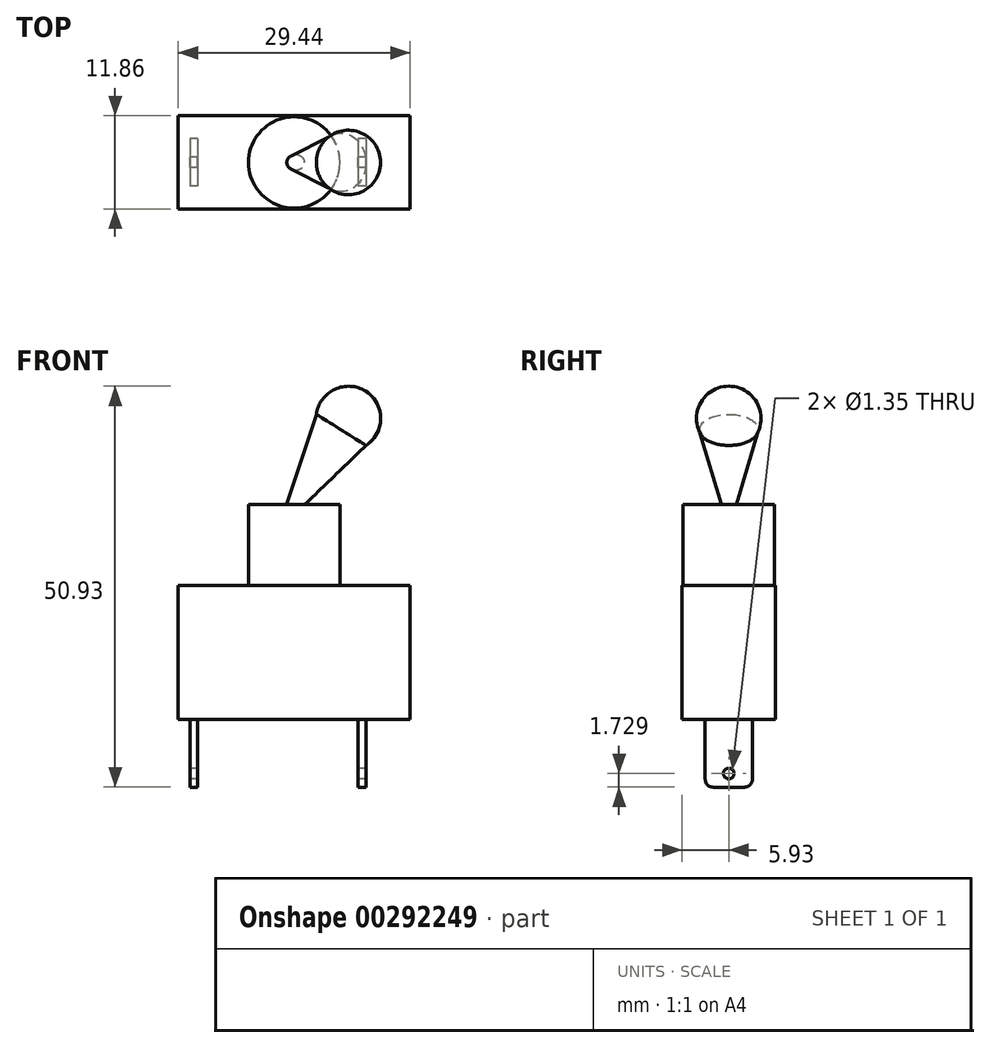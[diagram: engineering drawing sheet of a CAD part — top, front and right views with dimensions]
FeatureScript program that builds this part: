
annotation { "Feature Type Name" : "Feature", "Feature Type Description" : "" }
export const myFeature = defineFeature(function(context is Context, id is Id, definition is map)
    precondition{}
    {
        {
            var Q0;
            Q0=qCreatedBy(makeId("Front.planeOp"),FACE);
            var sketch = newSketch(context, id + "F0", { "sketchPlane" : qUnion([Q0])});
            skLineSegment(sketch, "E0.bottom", {"start": v(14.72, -8.52) * mm, "end": v(-14.72, -8.52) * mm});
            skLineSegment(sketch, "E0.top", {"start": v(14.72, 8.52) * mm, "end": v(-14.72, 8.52) * mm});
            skLineSegment(sketch, "E0.left", {"start": v(14.72, -8.52) * mm, "end": v(14.72, 8.52) * mm});
            skLineSegment(sketch, "E0.right", {"start": v(-14.72, -8.52) * mm, "end": v(-14.72, 8.52) * mm});
            skPoint(sketch, "E0.middle", {"position": v(0, 0) * mm});
            skSolve(sketch);
        }
        {
            var Q0;
            Q0 = qSketchRegion(id + "F0", true);
            extrude(context, id + "F1", {"entities" : qUnion([Q0]), "endBound" : BoundingType.SYMMETRIC, "depth" : 11.86 * mm});
        }
        {
            var Q0;
            Q0=makeQuery(id+"F1.opExtrude","SWEPT_FACE",FACE,{"disambiguationData":[OSD([sQuery(id+"F0.wireOp",EDGE,"E0.top")])]});
            var sketch = newSketch(context, id + "F2", { "sketchPlane" : qUnion([Q0])});
            skCircle(sketch, "E1", {"center": v(0, 0) * mm, "radius": 5.8 * mm});
            skSolve(sketch);
        }
        {
            var Q0;
            Q0 = qSketchRegion(id + "F2", true);
            extrude(context, id + "F3", {"entities" : qUnion([Q0]), "depth" : 10.26 * mm});
        }
        {
            var Q0;
            Q0=qCreatedBy(makeId("Front.planeOp"),FACE);
            var sketch = newSketch(context, id + "F4", { "sketchPlane" : qUnion([Q0])});
            skLineSegment(sketch, "E2", {"start": v(0, 18.75) * mm, "end": v(9.07, 33.18) * mm});
            skArc(sketch, "E3", {"start": v(9.07, 33.18) * mm, "mid": v(5.14, 33.42) * mm, "end": v(2.83, 30.24) * mm});
            skLineSegment(sketch, "E4", {"start": v(2.83, 30.24) * mm, "end": v(-1, 18.63) * mm});
            skLineSegment(sketch, "E5", {"start": v(0, 18.75) * mm, "end": v(-0.95, 18.75) * mm});
            skSolve(sketch);
        }
        {
            var Q0;
            Q0 = qSketchRegion(id + "F4", true);
            var Q1;
            Q1=sQuery(id+"F4.wireOp",EDGE,"E2");
            revolve(context, id + "F5", {"operationType" : NewBodyOperationType.ADD, "entities" : qUnion([Q0]), "axis" : qUnion([Q1]), "revolveType" : RevolveType.FULL});
        }
        {
            var Q0;
            Q0=makeQuery(id+"F1.opExtrude","SWEPT_FACE",FACE,{"disambiguationData":[OSD([sQuery(id+"F0.wireOp",EDGE,"E0.bottom")])]});
            var sketch = newSketch(context, id + "F6", { "sketchPlane" : qUnion([Q0])});
            skLineSegment(sketch, "E6.bottom", {"start": v(9.14, -3) * mm, "end": v(8.14, -3) * mm});
            skLineSegment(sketch, "E6.top", {"start": v(9.14, 3) * mm, "end": v(8.14, 3) * mm});
            skLineSegment(sketch, "E6.left", {"start": v(9.14, -3) * mm, "end": v(9.14, 3) * mm});
            skLineSegment(sketch, "E6.right", {"start": v(8.14, -3) * mm, "end": v(8.14, 3) * mm});
            skPoint(sketch, "E6.middle", {"position": v(8.64, 0) * mm});
            skPoint(sketch, "E6.middle.positionSnap0", {"position": v(14.72, 0) * mm});
            skPoint(sketch, "E6.centerSnap0", {"position": v(14.72, 0) * mm});
            skLineSegment(sketch, "E7.bottom", {"start": v(-12.26, -3) * mm, "end": v(-13.26, -3) * mm});
            skLineSegment(sketch, "E7.top", {"start": v(-12.26, 3) * mm, "end": v(-13.26, 3) * mm});
            skLineSegment(sketch, "E7.left", {"start": v(-12.26, -3) * mm, "end": v(-12.26, 3) * mm});
            skLineSegment(sketch, "E7.right", {"start": v(-13.26, -3) * mm, "end": v(-13.26, 3) * mm});
            skPoint(sketch, "E7.middle", {"position": v(-12.76, 0) * mm});
            skPoint(sketch, "E7.middle.positionSnap0", {"position": v(-14.72, 0) * mm});
            skPoint(sketch, "E7.centerSnap0", {"position": v(-14.72, 0) * mm});
            skSolve(sketch);
        }
        {
            var Q0;
            Q0 = qSketchRegion(id + "F6", true);
            extrude(context, id + "F7", {"entities" : qUnion([Q0]), "depth" : 8.6 * mm});
        }
        {
            var Q0;
            Q0=makeQuery(id+"F7.opExtrude","CAP_EDGE",EDGE,{"disambiguationData":[OSD([sQuery(id+"F6.wireOp",EDGE,"E6.bottom")])],"isStart":false});
            var Q1;
            Q1=makeQuery(id+"F7.opExtrude","CAP_EDGE",EDGE,{"disambiguationData":[OSD([sQuery(id+"F6.wireOp",EDGE,"E6.top")])],"isStart":false});
            var Q2;
            Q2=makeQuery(id+"F7.opExtrude","CAP_EDGE",EDGE,{"disambiguationData":[OSD([sQuery(id+"F6.wireOp",EDGE,"E7.top")])],"isStart":false});
            var Q3;
            Q3=makeQuery(id+"F7.opExtrude","CAP_EDGE",EDGE,{"disambiguationData":[OSD([sQuery(id+"F6.wireOp",EDGE,"E7.bottom")])],"isStart":false});
            fillet(context, id + "F8", {"entities" : qUnion([Q0, Q1, Q2, Q3]), "radius" : 1 * mm, "tangentPropagation" : true, "allowEdgeOverflow" : false});
        }
        {
            var Q0;
            Q0=makeQuery(id+"F7.opExtrude","SWEPT_FACE",FACE,{"disambiguationData":[OSD([sQuery(id+"F6.wireOp",EDGE,"E7.right")])]});
            var sketch = newSketch(context, id + "F9", { "sketchPlane" : qUnion([Q0])});
            skCircle(sketch, "E8", {"center": v(0, -15.4) * mm, "radius": 0.68 * mm});
            skPoint(sketch, "E8.centerSnap0", {"position": v(0, -17.12) * mm});
            skSolve(sketch);
        }
        {
            var Q0;
            Q0 = qSketchRegion(id + "F9", true);
            extrude(context, id + "F10", {"entities" : qUnion([Q0]), "operationType" : NewBodyOperationType.REMOVE, "oppositeDirection" : true, "depth" : 500 * mm});
        }
    });
